FCSTD DOCUMENT  (FreeCAD 0.19R)
Label: logo_sketch_constrained
License: All rights reserved
LicenseURL: http://en.wikipedia.org/wiki/All_rights_reserved
objects: Sketcher::SketchObject×4
note: 4 computed .brp shape members not serialized (recipe doc carries the construction recipe); baked Part::Feature solids carry a one-line shape summary decoded from their .brp

FEATURE [Sketcher::SketchObject] Sketch001
  FullyConstrained = false
  sketch-geometry (16):
    g0: LineSegment StartX=3.76563 StartY=285.298 StartZ=0 EndX=5.41563 EndY=285.298 EndZ=0
    g1: LineSegment StartX=5.41563 StartY=285.298 StartZ=0 EndX=5.41563 EndY=283.598 EndZ=0
    g2: LineSegment StartX=11.1056 StartY=283.598 StartZ=0 EndX=11.1056 EndY=285.298 EndZ=0
    g3: LineSegment StartX=11.1056 StartY=285.298 StartZ=0 EndX=12.7556 EndY=285.298 EndZ=0
    g4: LineSegment StartX=9.45063 StartY=293.128 StartZ=0 EndX=9.45063 EndY=292.178 EndZ=0
    g5: LineSegment StartX=9.45063 StartY=292.178 StartZ=0 EndX=7.07063 EndY=292.178 EndZ=0
    g6: LineSegment StartX=7.07063 StartY=292.178 StartZ=0 EndX=7.07063 EndY=293.128 EndZ=0
    g7: ArcOfCircle CenterX=8.26063 CenterY=288.013 CenterZ=0 NormalX=0 NormalY=0 NormalZ=1 AngleXU=0 Radius=8.08582 StartAngle=4.71239 EndAngle=10.4888
    g8: ArcOfCircle CenterX=8.26063 CenterY=288.013 CenterZ=0 NormalX=0 NormalY=0 NormalZ=1 AngleXU=0 Radius=5.25141 StartAngle=1.79939 EndAngle=3.68498
    g9: ArcOfCircle CenterX=8.26063 CenterY=288.013 CenterZ=0 NormalX=0 NormalY=0 NormalZ=1 AngleXU=0 Radius=5.25141 StartAngle=5.73979 EndAngle=7.62539
    g10: ArcOfCircle CenterX=8.26063 CenterY=288.013 CenterZ=0 NormalX=0 NormalY=0 NormalZ=1 AngleXU=0 Radius=5.25243 StartAngle=4.13998 EndAngle=5.28479
    g11: LineSegment StartX=4.33631 StartY=280.944 StartZ=0 EndX=4.33631 EndY=284.219 EndZ=0
    g12: LineSegment StartX=4.33631 StartY=280.944 StartZ=0 EndX=1.06115 EndY=280.944 EndZ=0
    g13: LineSegment StartX=4.33631 StartY=284.219 StartZ=0 EndX=4.33631 EndY=285.298 EndZ=0
    g14: LineSegment StartX=4.33631 StartY=284.219 StartZ=0 EndX=5.41563 EndY=284.219 EndZ=0
    g15: LineSegment StartX=4.33631 StartY=284.219 StartZ=0 EndX=4.33631 EndY=283.598 EndZ=0
  constraints (46):
    c: Coincident(g7,g11)
    c: Coincident(g12,g7)
    c: Vertical(g11)
    c: Horizontal(g12)
    c: Equal(g11,g12)
    c: Coincident(g0,g1)
    c: Coincident(g2,g3)
    c: Coincident(g2,g10)
    c: Coincident(g1,g10)
    c: Coincident(g0,g8)
    c: Coincident(g5,g6)
    c: Coincident(g4,g5)
    c: Coincident(g6,g8)
    c: Coincident(g4,g9)
    c: Horizontal(g4,g6)
    c: Horizontal(g5)
    c: Coincident(g3,g9)
    c: Equal(g0,g3)
    c: Vertical(g1)
    c: Vertical(g2)
    c: Horizontal(g3)
    c: Horizontal(g0)
    c: Equal(g1,g2)
    c: Horizontal(g2,g1)
    c: DistanceX(g0,g0) = 1.65
    c: DistanceY(g2,g2) = 1.7
    c: DistanceX(g5,g5) = 2.38
    c: DistanceY(g4,g4) = 0.95
    c: Vertical(g4)
    c: DistanceX(g0,g2) = 5.69
    c: Vertical(g6)
    c: DistanceY(g2,g4) = 6.88
    c: Coincident(g7,g8)
    c: Coincident(g7,g9)
    c: Coincident(g7,g10)
    c: Horizontal(g14)
    c: Vertical(g13)
    c: Equal(g13,g14)
    c: Coincident(g11,g13)
    c: Coincident(g11,g14)
    c: PointOnObject(g14,g1)
    c: PointOnObject(g13,g0)
    c: Vertical(g7,g7)
    c: PointOnObject(g15,g11)
    c: Coincident(g15,g11)
    c: Horizontal(g15,g1)
FEATURE [Sketcher::SketchObject] Sketch002
  FullyConstrained = false
  sketch-geometry (21):
    g0: LineSegment StartX=3.90561 StartY=285.29 StartZ=0 EndX=5.55561 EndY=285.29 EndZ=0
    g1: LineSegment StartX=5.55561 StartY=285.29 StartZ=0 EndX=5.55561 EndY=283.59 EndZ=0
    g2: LineSegment StartX=11.2456 StartY=283.59 StartZ=0 EndX=11.2456 EndY=285.29 EndZ=0
    g3: LineSegment StartX=11.2456 StartY=285.29 StartZ=0 EndX=12.8956 EndY=285.29 EndZ=0
    g4: LineSegment StartX=9.59061 StartY=293.12 StartZ=0 EndX=9.59061 EndY=292.17 EndZ=0
    g5: LineSegment StartX=9.59061 StartY=292.17 StartZ=0 EndX=7.21061 EndY=292.17 EndZ=0
    g6: LineSegment StartX=7.21061 StartY=292.17 StartZ=0 EndX=7.21061 EndY=293.12 EndZ=0
    g7: ArcOfCircle CenterX=8.40061 CenterY=288.005 CenterZ=0 NormalX=0 NormalY=0 NormalZ=1 AngleXU=0 Radius=5.25141 StartAngle=1.79939 EndAngle=3.68498
    g8: ArcOfCircle CenterX=8.40061 CenterY=288.005 CenterZ=0 NormalX=0 NormalY=0 NormalZ=1 AngleXU=0 Radius=5.25141 StartAngle=5.73979 EndAngle=7.62539
    g9: ArcOfCircle CenterX=8.40061 CenterY=288.005 CenterZ=0 NormalX=0 NormalY=0 NormalZ=1 AngleXU=0 Radius=5.25243 StartAngle=4.13998 EndAngle=5.28479
    g10: ArcOfCircle CenterX=8.40061 CenterY=288.005 CenterZ=0 NormalX=0 NormalY=0 NormalZ=1 AngleXU=0 Radius=7.65873 StartAngle=4.71239 EndAngle=10.2434
    g11: ArcOfCircle CenterX=8.40061 CenterY=288.005 CenterZ=0 NormalX=0 NormalY=0 NormalZ=1 AngleXU=0 Radius=9.14654 StartAngle=4.71239 EndAngle=10.238
    g12: LineSegment StartX=8.40061 StartY=280.346 StartZ=0 EndX=8.40061 EndY=278.858 EndZ=0
    g13: LineSegment StartX=3.1678 StartY=282.413 StartZ=0 EndX=3.1678 EndY=284.39 EndZ=0
    g14: LineSegment StartX=3.1678 StartY=284.39 StartZ=0 EndX=4.6556 EndY=284.39 EndZ=0
    g15: LineSegment StartX=4.6556 StartY=284.39 StartZ=0 EndX=4.6556 EndY=279.872 EndZ=0
    g16: LineSegment StartX=4.6556 StartY=279.872 StartZ=0 EndX=0.138176 EndY=279.872 EndZ=0
    g17: LineSegment StartX=0.138176 StartY=279.872 StartZ=0 EndX=0.138176 EndY=281.36 EndZ=0
    g18: LineSegment StartX=0.138176 StartY=281.36 StartZ=0 EndX=2.11527 EndY=281.36 EndZ=0
    g19: LineSegment StartX=4.6556 StartY=284.39 StartZ=0 EndX=4.6556 EndY=285.29 EndZ=0
    g20: LineSegment StartX=4.6556 StartY=284.39 StartZ=0 EndX=5.55561 EndY=284.39 EndZ=0
  constraints (59):
    c: Coincident(g0,g1)
    c: Coincident(g2,g3)
    c: Coincident(g2,g9)
    c: Coincident(g1,g9)
    c: Coincident(g0,g7)
    c: Coincident(g5,g6)
    c: Coincident(g4,g5)
    c: Coincident(g6,g7)
    c: Coincident(g4,g8)
    c: Horizontal(g4,g6)
    c: Horizontal(g5)
    c: Coincident(g3,g8)
    c: Equal(g0,g3)
    c: Vertical(g1)
    c: Vertical(g2)
    c: Horizontal(g3)
    c: Horizontal(g0)
    c: Equal(g1,g2)
    c: Horizontal(g2,g1)
    c: DistanceX(g0,g0) = 1.65
    c: DistanceY(g2,g2) = 1.7
    c: DistanceX(g5,g5) = 2.38
    c: DistanceY(g4,g4) = 0.95
    c: Vertical(g4)
    c: DistanceX(g0,g2) = 5.69
    c: Vertical(g6)
    c: DistanceY(g2,g4) = 6.88
    c: Coincident(g7,g8)
    c: Coincident(g7,g9)
    c: Coincident(g7,g10)
    c: Coincident(g7,g11)
    c: Coincident(g11,g12)
    c: Coincident(g10,g12)
    c: Vertical(g10,g7)
    c: Vertical(g12)
    c: Coincident(g13,g10)
    c: Vertical(g13)
    c: Coincident(g13,g14)
    c: Vertical(g15)
    c: Coincident(g15,g16)
    c: Horizontal(g16)
    c: Coincident(g16,g17)
    c: Vertical(g17)
    c: Coincident(g17,g18)
    c: Coincident(g18,g11)
    c: Coincident(g14,g15)
    c: Horizontal(g14)
    c: Horizontal(g18)
    c: Equal(g17,g14)
    c: Equal(g16,g15)
    c: Equal(g13,g18)
    c: Equal(g14,g12)
    c: Coincident(g19,g14)
    c: PointOnObject(g19,g0)
    c: Vertical(g19)
    c: Coincident(g20,g14)
    c: PointOnObject(g20,g1)
    c: Horizontal(g20)
    c: Equal(g20,g19)
FEATURE [Sketcher::SketchObject] Sketch003
  FullyConstrained = false
  sketch-geometry (21):
    g0: LineSegment StartX=3.60089 StartY=285.245 StartZ=0 EndX=5.25089 EndY=285.245 EndZ=0
    g1: LineSegment StartX=5.25089 StartY=285.245 StartZ=0 EndX=5.25089 EndY=283.545 EndZ=0
    g2: LineSegment StartX=10.9409 StartY=283.545 StartZ=0 EndX=10.9409 EndY=285.245 EndZ=0
    g3: LineSegment StartX=10.9409 StartY=285.245 StartZ=0 EndX=12.5909 EndY=285.245 EndZ=0
    g4: LineSegment StartX=9.28589 StartY=293.075 StartZ=0 EndX=9.28589 EndY=292.125 EndZ=0
    g5: LineSegment StartX=9.28589 StartY=292.125 StartZ=0 EndX=6.90589 EndY=292.125 EndZ=0
    g6: LineSegment StartX=6.90589 StartY=292.125 StartZ=0 EndX=6.90589 EndY=293.075 EndZ=0
    g7: ArcOfCircle CenterX=8.09589 CenterY=287.96 CenterZ=0 NormalX=0 NormalY=0 NormalZ=1 AngleXU=0 Radius=5.25141 StartAngle=1.79939 EndAngle=3.68498
    g8: ArcOfCircle CenterX=8.09589 CenterY=287.96 CenterZ=0 NormalX=0 NormalY=0 NormalZ=1 AngleXU=0 Radius=5.25141 StartAngle=5.73979 EndAngle=7.62539
    g9: ArcOfCircle CenterX=8.09589 CenterY=287.96 CenterZ=0 NormalX=0 NormalY=0 NormalZ=1 AngleXU=0 Radius=5.25243 StartAngle=4.13998 EndAngle=5.28479
    g10: ArcOfCircle CenterX=8.09589 CenterY=287.96 CenterZ=0 NormalX=0 NormalY=0 NormalZ=1 AngleXU=0 Radius=7.89505 StartAngle=4.71239 EndAngle=10.3059
    g11: ArcOfCircle CenterX=8.09589 CenterY=287.96 CenterZ=0 NormalX=0 NormalY=0 NormalZ=1 AngleXU=0 Radius=8.89505 StartAngle=4.71239 EndAngle=10.2951
    g12: LineSegment StartX=8.09589 StartY=280.065 StartZ=0 EndX=8.09589 EndY=279.065 EndZ=0
    g13: LineSegment StartX=3.07229 StartY=281.869 StartZ=0 EndX=3.07229 EndY=284.066 EndZ=0
    g14: LineSegment StartX=3.07229 StartY=284.066 StartZ=0 EndX=4.07229 EndY=284.066 EndZ=0
    g15: LineSegment StartX=4.07229 StartY=284.066 StartZ=0 EndX=4.07229 EndY=280.159 EndZ=0
    g16: LineSegment StartX=4.07229 StartY=280.159 StartZ=0 EndX=0.165521 EndY=280.159 EndZ=0
    g17: LineSegment StartX=0.165521 StartY=280.159 StartZ=0 EndX=0.165521 EndY=281.159 EndZ=0
    g18: LineSegment StartX=0.165521 StartY=281.159 StartZ=0 EndX=2.3623 EndY=281.159 EndZ=0
    g19: LineSegment StartX=4.07229 StartY=284.066 StartZ=0 EndX=4.07229 EndY=285.245 EndZ=0
    g20: LineSegment StartX=4.07229 StartY=284.066 StartZ=0 EndX=5.25089 EndY=284.066 EndZ=0
  constraints (60):
    c: Coincident(g0,g1)
    c: Coincident(g2,g3)
    c: Coincident(g2,g9)
    c: Coincident(g1,g9)
    c: Coincident(g0,g7)
    c: Coincident(g5,g6)
    c: Coincident(g4,g5)
    c: Coincident(g6,g7)
    c: Coincident(g4,g8)
    c: Horizontal(g4,g6)
    c: Horizontal(g5)
    c: Coincident(g3,g8)
    c: Equal(g0,g3)
    c: Vertical(g1)
    c: Vertical(g2)
    c: Horizontal(g3)
    c: Horizontal(g0)
    c: Equal(g1,g2)
    c: Horizontal(g2,g1)
    c: DistanceX(g0,g0) = 1.65
    c: DistanceY(g2,g2) = 1.7
    c: DistanceX(g5,g5) = 2.38
    c: DistanceY(g4,g4) = 0.95
    c: Vertical(g4)
    c: DistanceX(g0,g2) = 5.69
    c: Vertical(g6)
    c: DistanceY(g2,g4) = 6.88
    c: Coincident(g7,g8)
    c: Coincident(g7,g9)
    c: Coincident(g7,g10)
    c: Coincident(g7,g11)
    c: Coincident(g11,g12)
    c: Coincident(g10,g12)
    c: Vertical(g10,g7)
    c: Vertical(g12)
    c: Coincident(g13,g10)
    c: Vertical(g13)
    c: Coincident(g13,g14)
    c: Vertical(g15)
    c: Coincident(g15,g16)
    c: Horizontal(g16)
    c: Coincident(g16,g17)
    c: Vertical(g17)
    c: Coincident(g17,g18)
    c: Coincident(g18,g11)
    c: Coincident(g14,g15)
    c: Horizontal(g14)
    c: Horizontal(g18)
    c: Equal(g17,g14)
    c: Equal(g16,g15)
    c: Equal(g13,g18)
    c: Equal(g14,g12)
    c: Coincident(g19,g14)
    c: PointOnObject(g19,g0)
    c: Vertical(g19)
    c: Coincident(g20,g14)
    c: PointOnObject(g20,g1)
    c: Horizontal(g20)
    c: Equal(g20,g19)
    c: DistanceY(g17,g17) = 1
FEATURE [Sketcher::SketchObject] Sketch004
  FullyConstrained = false
  sketch-geometry (21):
    g0: LineSegment StartX=3.2301 StartY=284.865 StartZ=0 EndX=4.8801 EndY=284.865 EndZ=0
    g1: LineSegment StartX=4.8801 StartY=284.865 StartZ=0 EndX=4.8801 EndY=283.165 EndZ=0
    g2: LineSegment StartX=10.5701 StartY=283.165 StartZ=0 EndX=10.5701 EndY=284.865 EndZ=0
    g3: LineSegment StartX=10.5701 StartY=284.865 StartZ=0 EndX=12.2201 EndY=284.865 EndZ=0
    g4: LineSegment StartX=8.9151 StartY=292.695 StartZ=0 EndX=8.9151 EndY=291.745 EndZ=0
    g5: LineSegment StartX=8.9151 StartY=291.745 StartZ=0 EndX=6.5351 EndY=291.745 EndZ=0
    g6: LineSegment StartX=6.5351 StartY=291.745 StartZ=0 EndX=6.5351 EndY=292.695 EndZ=0
    g7: ArcOfCircle CenterX=7.7251 CenterY=287.58 CenterZ=0 NormalX=0 NormalY=0 NormalZ=1 AngleXU=0 Radius=5.25141 StartAngle=1.79939 EndAngle=3.68498
    g8: ArcOfCircle CenterX=7.7251 CenterY=287.58 CenterZ=0 NormalX=0 NormalY=0 NormalZ=1 AngleXU=0 Radius=5.25141 StartAngle=5.73979 EndAngle=7.62539
    g9: ArcOfCircle CenterX=7.7251 CenterY=287.58 CenterZ=0 NormalX=0 NormalY=0 NormalZ=1 AngleXU=0 Radius=5.25243 StartAngle=4.13998 EndAngle=5.28479
    g10: ArcOfCircle CenterX=7.7251 CenterY=287.58 CenterZ=0 NormalX=0 NormalY=0 NormalZ=1 AngleXU=0 Radius=8.04249 StartAngle=4.71239 EndAngle=10.2977
    g11: ArcOfCircle CenterX=7.7251 CenterY=287.58 CenterZ=0 NormalX=0 NormalY=0 NormalZ=1 AngleXU=0 Radius=9.29249 StartAngle=4.71239 EndAngle=10.2859
    g12: LineSegment StartX=7.7251 StartY=279.538 StartZ=0 EndX=7.7251 EndY=278.288 EndZ=0
    g13: LineSegment StartX=2.55699 StartY=281.418 StartZ=0 EndX=2.55699 EndY=283.792 EndZ=0
    g14: LineSegment StartX=2.55699 StartY=283.792 StartZ=0 EndX=3.80699 EndY=283.792 EndZ=0
    g15: LineSegment StartX=3.80699 StartY=283.792 StartZ=0 EndX=3.80699 EndY=279.281 EndZ=0
    g16: LineSegment StartX=3.80699 StartY=279.281 StartZ=0 EndX=-0.703676 EndY=279.281 EndZ=0
    g17: LineSegment StartX=-0.703676 StartY=279.281 StartZ=0 EndX=-0.703676 EndY=280.531 EndZ=0
    g18: LineSegment StartX=-0.703676 StartY=280.531 StartZ=0 EndX=1.67017 EndY=280.531 EndZ=0
    g19: LineSegment StartX=3.80699 StartY=283.792 StartZ=0 EndX=3.80699 EndY=284.865 EndZ=0
    g20: LineSegment StartX=3.80699 StartY=283.792 StartZ=0 EndX=4.8801 EndY=283.792 EndZ=0
  constraints (60):
    c: Coincident(g0,g1)
    c: Coincident(g2,g3)
    c: Coincident(g2,g9)
    c: Coincident(g1,g9)
    c: Coincident(g0,g7)
    c: Coincident(g5,g6)
    c: Coincident(g4,g5)
    c: Coincident(g6,g7)
    c: Coincident(g4,g8)
    c: Horizontal(g4,g6)
    c: Horizontal(g5)
    c: Coincident(g3,g8)
    c: Equal(g0,g3)
    c: Vertical(g1)
    c: Vertical(g2)
    c: Horizontal(g3)
    c: Horizontal(g0)
    c: Equal(g1,g2)
    c: Horizontal(g2,g1)
    c: DistanceX(g0,g0) = 1.65
    c: DistanceY(g2,g2) = 1.7
    c: DistanceX(g5,g5) = 2.38
    c: DistanceY(g4,g4) = 0.95
    c: Vertical(g4)
    c: DistanceX(g0,g2) = 5.69
    c: Vertical(g6)
    c: DistanceY(g2,g4) = 6.88
    c: Coincident(g7,g8)
    c: Coincident(g7,g9)
    c: Coincident(g7,g10)
    c: Coincident(g7,g11)
    c: Coincident(g11,g12)
    c: Coincident(g10,g12)
    c: Vertical(g10,g7)
    c: Vertical(g12)
    c: Coincident(g13,g10)
    c: Vertical(g13)
    c: Coincident(g13,g14)
    c: Vertical(g15)
    c: Coincident(g15,g16)
    c: Horizontal(g16)
    c: Coincident(g16,g17)
    c: Vertical(g17)
    c: Coincident(g17,g18)
    c: Coincident(g18,g11)
    c: Coincident(g14,g15)
    c: Horizontal(g14)
    c: Horizontal(g18)
    c: Equal(g17,g14)
    c: Equal(g16,g15)
    c: Equal(g13,g18)
    c: Equal(g14,g12)
    c: Coincident(g19,g14)
    c: PointOnObject(g19,g0)
    c: Vertical(g19)
    c: Coincident(g20,g14)
    c: PointOnObject(g20,g1)
    c: Horizontal(g20)
    c: Equal(g20,g19)
    c: DistanceY(g17,g17) = 1.25
